# Revit family: VALVULA LIVIANA ROSCAR
name_source: partatom
category: Pipe Accessories
units: mm (PartAtom-declared; Revit-internal decimal feet)

## family parameters
Always vertical = Yes
Cut with Voids When Loaded = No
Part Type = Valve - Breaks Into
Round Connector Dimension = Use Diameter
Shared = No
Work Plane-Based = No

## types (7) — shared parameters
Description = VÁLVULAS DE BOLA ROSCAR ECO
Imagen = https://pcpplasticos.co
Manufacturer = PCP PLASTICOS
URL = https://pcpplasticos.co
zero-valued in all types: Default Elevation

## per-type parameters (varying)
| type | 1 1/2" | 1 1/4" | 1" | 1/2" | 2" | 3" | 3/4" | D | Model | SKU | d1 | d2 |
| Diametro 1/2" | No | No | No | Yes | No | No | No | 12.7 mm  [stored 0.0416667 ft] | 3062 | 3062 | 34.5 mm  [stored 0.113189 ft] | 33.7 mm  [stored 0.110564 ft] |
| Diametro 3/4" | No | No | No | No | No | No | Yes | 19.05 mm  [stored 0.0625 ft] | 3099 | 3099 | 42.294 mm | 41.494 mm  [stored 0.136135 ft] |
| Diametro 1" | No | No | Yes | No | No | No | No | 25.4 mm  [stored 0.0833333 ft] | 3101 | 3101 | 47 mm  [stored 0.154199 ft] | 46.2 mm  [stored 0.151575 ft] |
| Diametro 1 1/4" | No | Yes | No | No | No | No | No | 31.8 mm  [stored 0.104331 ft] | 3305 | 3305 | 53.35 mm  [stored 0.175033 ft] | 52.55 mm  [stored 0.172408 ft] |
| Diametro 1 1/2" | Yes | No | No | No | No | No | No | 38.1 mm  [stored 0.125 ft] | 3307 | 3307 | 59.5 mm  [stored 0.19521 ft] | 58.7 mm  [stored 0.192585 ft] |
| Diametro 2" | No | No | No | No | Yes | No | No | 50.8 mm  [stored 0.166667 ft] | 3309 | 3309 | 65.5 mm | 64.7 mm  [stored 0.21227 ft] |
| Diametro 3" | No | No | No | No | No | Yes | No | 76.2 mm  [stored 0.25 ft] | 3312 | 3312 | 107.5 mm | 106.7 mm  [stored 0.350066 ft] |

note: [stored X ft] marks values corroborated as IEEE doubles in the binary element streams (Revit-internal decimal feet)

## geometry (parser evidence)
native form markers: Sweep x2
no freeform markers — native parametric forms only
